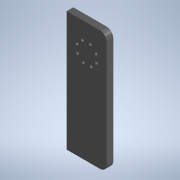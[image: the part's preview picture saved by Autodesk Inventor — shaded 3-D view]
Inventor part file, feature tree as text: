
AUTODESK INVENTOR PART (.ipt)
format: ipt  version: 2021 (Build 250183000, 183)  size: 125,440 bytes
history: native  units: mm (DEFAULTED — no unit token found)
features: sketch x3, extrude x2, fillet x1, other x1
ambient origin geometry x8: Origin, YZ Plane, XZ Plane, XY Plane, X Axis, Y Axis, Z Axis, Center Point
bodies: Solid1 (feature_tree)
feature tree (7):
  extrude  "Extrusion1"  Depth=6.35mm TaperAngle=0.0deg
  fillet  "Fillet1"  Radius=6.35mm
  extrude  "Extrusion7"  Depth=2.7178mm
  sketch  "Sketch9"  dims[d62=9.779mm d63=80.0mm d65=360.0deg d67=25.4mm d68=0.0mm d69=16.8402mm d70=8.4201mm d71=8.4201mm d86=38.1mm d87=88.9mm]
  other  "Work Axis1"
  sketch  "Sketch1"  dims[d0=114.3mm d2=6.35mm d3=0.0mm d4=6.35mm]
  sketch  "Sketch8"  dims[d60=5.08mm d61=2.7178mm]
